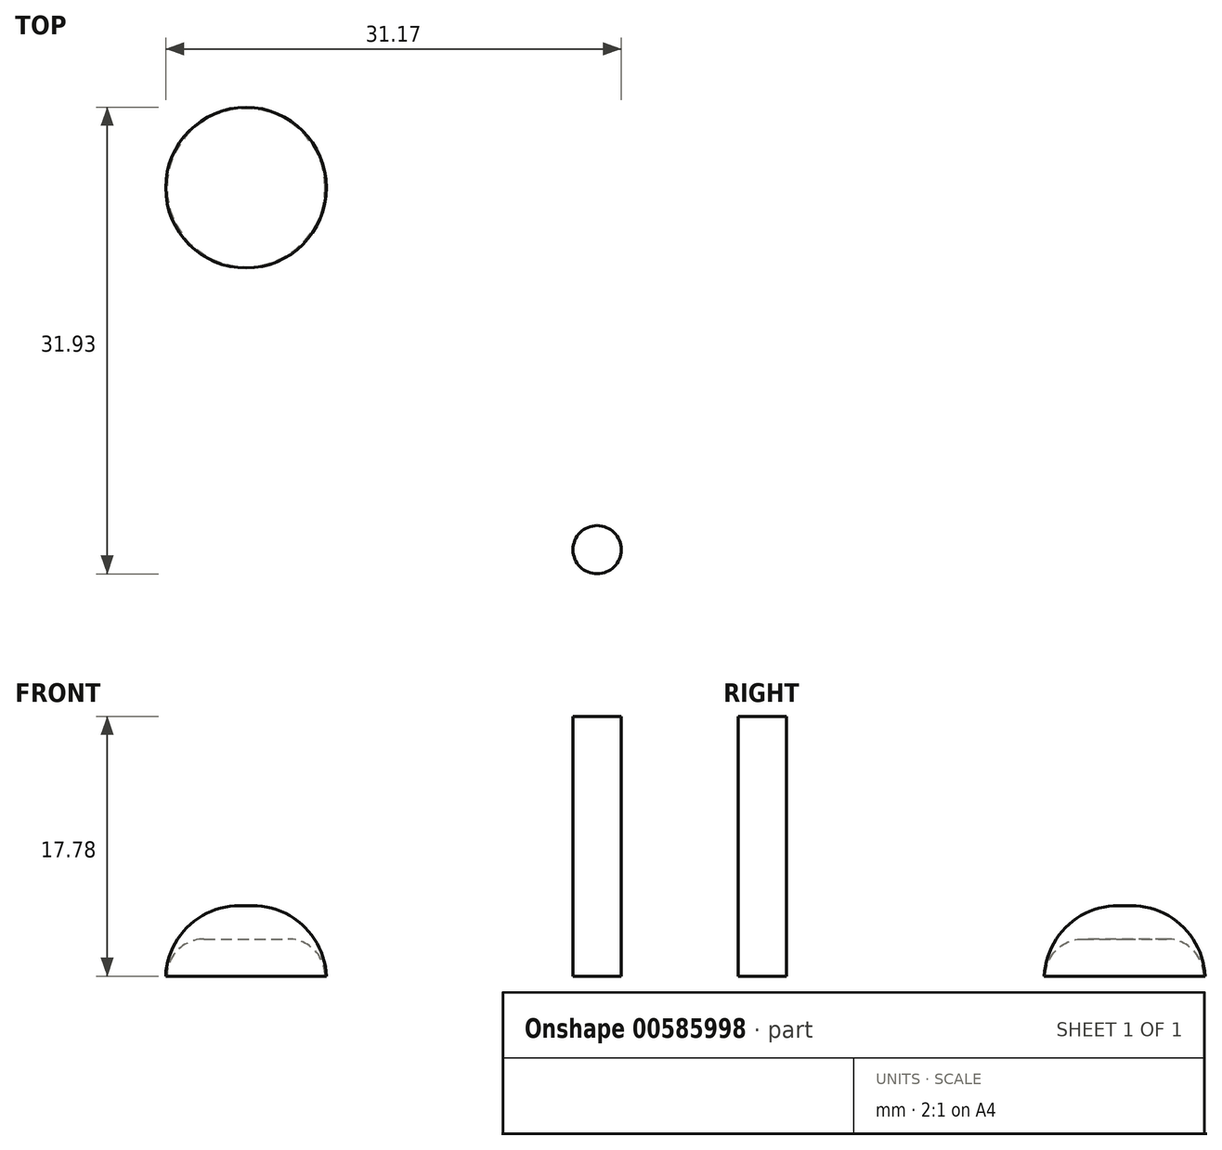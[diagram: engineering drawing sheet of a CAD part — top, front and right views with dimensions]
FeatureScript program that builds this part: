
annotation { "Feature Type Name" : "Feature", "Feature Type Description" : "" }
export const myFeature = defineFeature(function(context is Context, id is Id, definition is map)
    precondition{}
    {
        {
            var Q0;
            Q0=qCreatedBy(makeId("Top.planeOp"),FACE);
            var sketch = newSketch(context, id + "F0", { "sketchPlane" : qUnion([Q0])});
            skCircle(sketch, "E0", {"center": v(-39, 23.95) * mm, "radius": 1.65 * mm});
            skSolve(sketch);
        }
        {
            var Q0;
            Q0 = qSketchRegion(id + "F0", true);
            extrude(context, id + "F1", {"entities" : qUnion([Q0]), "depth" : 17.78 * mm, "offsetDistance" : 25.4 * mm});
        }
        {
            var Q0;
            Q0=qCreatedBy(makeId("Top.planeOp"),FACE);
            var sketch = newSketch(context, id + "F2", { "sketchPlane" : qUnion([Q0])});
            skCircle(sketch, "E1", {"center": v(-63, 48.73) * mm, "radius": 5.5 * mm});
            skSolve(sketch);
        }
        {
            var Q0;
            Q0=makeQuery(id+"F2.imprint","IMPRINT",FACE,{"disambiguationData":[TD([[makeQuery(id+"F2.imprint","IMPRINT",EDGE,{"derivedFrom":sQuery(id+"F2.wireOp",EDGE,"E1")}),1.0]])]});
            extrude(context, id + "F3", {"entities" : qUnion([Q0]), "depth" : 4.83 * mm, "offsetDistance" : 25.4 * mm});
        }
        {
            var Q0;
            Q0=makeQuery(id+"F3.opExtrude","CAP_FACE",FACE,{"disambiguationData":[OSD([sQuery(id+"F2.wireOp",EDGE,"E1")])],"isStart":true});
            var sketch = newSketch(context, id + "F4", { "sketchPlane" : qUnion([Q0])});
            skCircle(sketch, "E2", {"center": v(-63, -48.73) * mm, "radius": 5.4 * mm});
            skSolve(sketch);
        }
        {
            var Q0;
            Q0 = qSketchRegion(id + "F4", true);
            extrude(context, id + "F5", {"entities" : qUnion([Q0]), "operationType" : NewBodyOperationType.REMOVE, "oppositeDirection" : true, "depth" : 2.54 * mm, "offsetDistance" : 25.4 * mm});
        }
        {
            var Q0;
            Q0=makeQuery(id+"F5.boolean.opBoolean","COPY",EDGE,{"derivedFrom":makeQuery(id+"F5.opExtrude","CAP_EDGE",EDGE,{"disambiguationData":[OSD([sQuery(id+"F4.wireOp",EDGE,"E2")])],"isStart":false})});
            fillet(context, id + "F6", {"entities" : qUnion([Q0]), "radius" : 2.54 * mm, "tangentPropagation" : true, "allowEdgeOverflow" : false});
        }
        {
            var Q0;
            Q0=makeQuery(id+"F3.opExtrude","CAP_EDGE",EDGE,{"disambiguationData":[OSD([sQuery(id+"F2.wireOp",EDGE,"E1")])],"isStart":false});
            fillet(context, id + "F7", {"entities" : qUnion([Q0]), "radius" : 5.08 * mm, "tangentPropagation" : true, "allowEdgeOverflow" : false});
        }
    });
